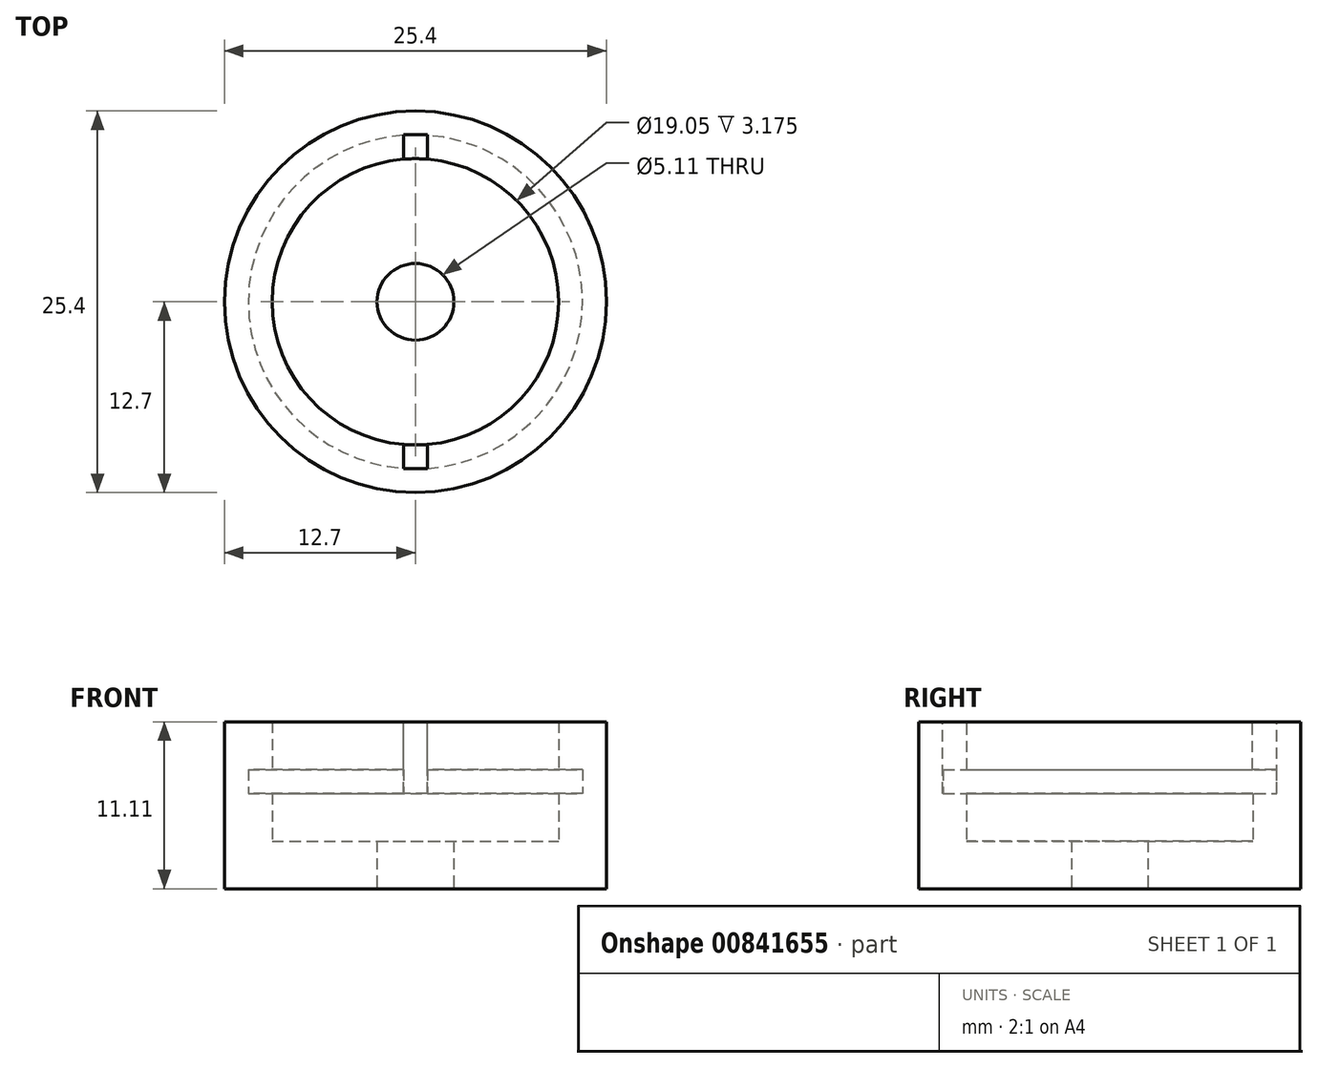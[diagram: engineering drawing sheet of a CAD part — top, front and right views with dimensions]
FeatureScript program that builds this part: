
annotation { "Feature Type Name" : "Feature", "Feature Type Description" : "" }
export const myFeature = defineFeature(function(context is Context, id is Id, definition is map)
    precondition{}
    {
        {
            var Q0;
            Q0=qCreatedBy(makeId("Right.planeOp"),FACE);
            var sketch = newSketch(context, id + "F0", { "sketchPlane" : qUnion([Q0])});
            skLineSegment(sketch, "E0.bottom", {"start": v(0, 0) * mm, "end": v(-9.53, 0) * mm});
            skLineSegment(sketch, "E0.top", {"start": v(0, 3.17) * mm, "end": v(-9.53, 3.17) * mm});
            skLineSegment(sketch, "E0.left", {"start": v(0, 0) * mm, "end": v(0, 3.17) * mm});
            skLineSegment(sketch, "E0.right", {"start": v(-9.53, 0) * mm, "end": v(-9.53, 3.17) * mm, "construction": true});
            skLineSegment(sketch, "E1.bottom", {"start": v(-9.53, 0) * mm, "end": v(-12.7, 0) * mm});
            skLineSegment(sketch, "E1.top", {"start": v(-9.53, 6.35) * mm, "end": v(-12.7, 6.35) * mm, "construction": true});
            skLineSegment(sketch, "E1.left", {"start": v(-9.53, 0) * mm, "end": v(-9.53, 6.35) * mm, "construction": true});
            skLineSegment(sketch, "E1.right", {"start": v(-12.7, 0) * mm, "end": v(-12.7, 6.35) * mm});
            skPoint(sketch, "E2.oppositeSnap0", {"position": v(-11.11, 6.35) * mm});
            skLineSegment(sketch, "E2.bottom", {"start": v(-12.7, 6.35) * mm, "end": v(-11.11, 6.35) * mm, "construction": true});
            skLineSegment(sketch, "E2.top", {"start": v(-12.7, 7.94) * mm, "end": v(-11.11, 7.94) * mm, "construction": true});
            skLineSegment(sketch, "E2.left", {"start": v(-12.7, 6.35) * mm, "end": v(-12.7, 7.94) * mm});
            skLineSegment(sketch, "E2.right", {"start": v(-11.11, 6.35) * mm, "end": v(-11.11, 7.94) * mm});
            skLineSegment(sketch, "E3.bottom", {"start": v(-12.7, 7.94) * mm, "end": v(-9.53, 7.94) * mm, "construction": true});
            skLineSegment(sketch, "E3.top", {"start": v(-12.7, 11.11) * mm, "end": v(-9.53, 11.11) * mm});
            skLineSegment(sketch, "E3.left", {"start": v(-12.7, 7.94) * mm, "end": v(-12.7, 11.11) * mm});
            skLineSegment(sketch, "E3.right", {"start": v(-9.53, 7.94) * mm, "end": v(-9.53, 11.11) * mm});
            skLineSegment(sketch, "E4", {"start": v(-9.53, 7.94) * mm, "end": v(-11.11, 7.94) * mm});
            skLineSegment(sketch, "E5", {"start": v(-11.11, 6.35) * mm, "end": v(-9.53, 6.35) * mm});
            skLineSegment(sketch, "E6", {"start": v(-9.53, 6.35) * mm, "end": v(-9.53, 3.17) * mm});
            skLineSegment(sketch, "E7", {"start": v(0, 0) * mm, "end": v(0, 10.8) * mm, "construction": true});
            skSolve(sketch);
        }
        {
            var Q0;
            Q0=makeQuery(id+"F0.imprint","IMPRINT",FACE,{"disambiguationData":[TD([[makeQuery(id+"F0.imprint","IMPRINT",EDGE,{"derivedFrom":sQuery(id+"F0.wireOp",EDGE,"E0.bottom")}),-1.0]])]});
            var Q1;
            Q1=sQuery(id+"F0.wireOp",EDGE,"E7");
            revolve(context, id + "F1", {"surfaceOperationType" : NewSurfaceOperationType.NEW, "entities" : qUnion([Q0]), "axis" : qUnion([Q1]), "revolveType" : RevolveType.FULL});
        }
        {
            var Q0;
            Q0=makeQuery(id+"F1.opRevolve","SWEPT_FACE",FACE,{"disambiguationData":[OSD([sQuery(id+"F0.wireOp",EDGE,"E3.top")])]});
            var sketch = newSketch(context, id + "F2", { "sketchPlane" : qUnion([Q0])});
            skLineSegment(sketch, "E8", {"start": v(12.7, 0) * mm, "end": v(-12.7, 0) * mm, "construction": true});
            skLineSegment(sketch, "E9", {"start": v(0, 12.7) * mm, "end": v(0, -12.7) * mm, "construction": true});
            skLineSegment(sketch, "E10", {"start": v(0, 9.53) * mm, "end": v(0.8, 9.53) * mm, "construction": true});
            skLineSegment(sketch, "E11", {"start": v(0.8, 9.5) * mm, "end": v(0.8, 11.11) * mm, "construction": true});
            skLineSegment(sketch, "E12.bottom", {"start": v(0.8, 9.5) * mm, "end": v(0, 9.5) * mm});
            skLineSegment(sketch, "E12.top", {"start": v(0.8, 11.11) * mm, "end": v(0, 11.11) * mm});
            skLineSegment(sketch, "E12.left", {"start": v(0.8, 9.5) * mm, "end": v(0.8, 11.11) * mm});
            skLineSegment(sketch, "E12.right", {"start": v(0, 9.5) * mm, "end": v(0, 11.11) * mm, "construction": true});
            skLineSegment(sketch, "E13.MirrorCS", {"start": v(-0.8, 9.5) * mm, "end": v(-0.8, 11.11) * mm});
            skLineSegment(sketch, "E14.MirrorCS", {"start": v(0, 9.53) * mm, "end": v(-0.8, 9.53) * mm, "construction": true});
            skLineSegment(sketch, "E15.MirrorCS", {"start": v(-0.8, 9.5) * mm, "end": v(-0.8, 11.11) * mm, "construction": true});
            skLineSegment(sketch, "E16.MirrorCS", {"start": v(-0.8, 9.5) * mm, "end": v(0, 9.5) * mm});
            skLineSegment(sketch, "E17.MirrorCS", {"start": v(-0.8, 11.11) * mm, "end": v(0, 11.11) * mm});
            skLineSegment(sketch, "E18.MirrorCS", {"start": v(-12.7, 0) * mm, "end": v(12.7, 0) * mm, "construction": true});
            skLineSegment(sketch, "E19.MirrorCS", {"start": v(0.8, -9.5) * mm, "end": v(0.8, -11.11) * mm});
            skLineSegment(sketch, "E20.MirrorCS", {"start": v(-0.8, -9.5) * mm, "end": v(-0.8, -11.11) * mm});
            skLineSegment(sketch, "E21.MirrorCS", {"start": v(-0.8, -11.11) * mm, "end": v(0, -11.11) * mm});
            skLineSegment(sketch, "E22.MirrorCS", {"start": v(0.8, -9.5) * mm, "end": v(0.8, -11.11) * mm, "construction": true});
            skLineSegment(sketch, "E23.MirrorCS", {"start": v(0.8, -9.5) * mm, "end": v(0, -9.5) * mm});
            skLineSegment(sketch, "E24.MirrorCS", {"start": v(-0.8, -9.5) * mm, "end": v(0, -9.5) * mm});
            skLineSegment(sketch, "E25.MirrorCS", {"start": v(0, -9.53) * mm, "end": v(-0.8, -9.53) * mm, "construction": true});
            skLineSegment(sketch, "E26.MirrorCS", {"start": v(0.8, -11.11) * mm, "end": v(0, -11.11) * mm});
            skLineSegment(sketch, "E27.MirrorCS", {"start": v(0, -9.5) * mm, "end": v(0, -11.11) * mm, "construction": true});
            skLineSegment(sketch, "E28.MirrorCS", {"start": v(-0.8, -9.5) * mm, "end": v(-0.8, -11.11) * mm, "construction": true});
            skLineSegment(sketch, "E29.MirrorCS", {"start": v(0, -9.53) * mm, "end": v(0.8, -9.53) * mm, "construction": true});
            skLineSegment(sketch, "E30.MirrorCS", {"start": v(0, -12.7) * mm, "end": v(0, 12.7) * mm, "construction": true});
            skSolve(sketch);
        }
        {
            var Q0;
            Q0 = qSketchRegion(id + "F2", true);
            extrude(context, id + "F3", {"entities" : qUnion([Q0]), "operationType" : NewBodyOperationType.REMOVE, "oppositeDirection" : true, "depth" : 4.76 * mm, "offsetDistance" : 25.4 * mm});
        }
        {
            var Q0;
            Q0=makeQuery(id+"F1.opRevolve","SWEPT_FACE",FACE,{"disambiguationData":[OSD([sQuery(id+"F0.wireOp",EDGE,"E0.bottom"),sQuery(id+"F0.wireOp",EDGE,"E1.bottom")])]});
            var sketch = newSketch(context, id + "F4", { "sketchPlane" : qUnion([Q0])});
            skPoint(sketch, "E31", {"position": v(0, 0) * mm});
            skSolve(sketch);
        }
        {
            var Q0;
            Q0=sQuery(id+"F4.wireOp",VERTEX,"E31");
            var Q1;
            Q1=makeQuery(id+"F1.opRevolve","SWEPT_BODY",BODY,{"disambiguationData":[OSD([sQuery(id+"F0.wireOp",EDGE,"E0.bottom"),sQuery(id+"F0.wireOp",EDGE,"E0.top"),sQuery(id+"F0.wireOp",EDGE,"E0.left"),sQuery(id+"F0.wireOp",EDGE,"E1.bottom"),sQuery(id+"F0.wireOp",EDGE,"E1.right"),sQuery(id+"F0.wireOp",EDGE,"E2.left"),sQuery(id+"F0.wireOp",EDGE,"E2.right"),sQuery(id+"F0.wireOp",EDGE,"E3.top"),sQuery(id+"F0.wireOp",EDGE,"E3.left"),sQuery(id+"F0.wireOp",EDGE,"E3.right"),sQuery(id+"F0.wireOp",EDGE,"E4"),sQuery(id+"F0.wireOp",EDGE,"E5"),sQuery(id+"F0.wireOp",EDGE,"E6")])]});
            hole(context, id + "F5", {"style" : HoleStyle.SIMPLE, "endStyle" : HoleEndStyle.THROUGH, "standardTappedOrClearance" : lookupTablePath({ "standard" : "ANSI", "engagement" : "75%", "pitch" : "20 tpi", "size" : "1/4", "type" : "Tapped" }), "standardBlindInLast" : lookupTablePath({ "standard" : "ANSI", "engagement" : "75%", "pitch" : "20 tpi", "size" : "1/4", "type" : "Tapped" }), "holeDiameter" : 5.1 * mm, "majorDiameter" : 6.35 * mm, "showTappedDepth" : true, "isTappedThrough" : true, "tappedDepth" : 12.7 * mm, "tapClearance" : 3, "locations" : qUnion([Q0]), "scope" : qUnion([Q1])});
        }
    });
